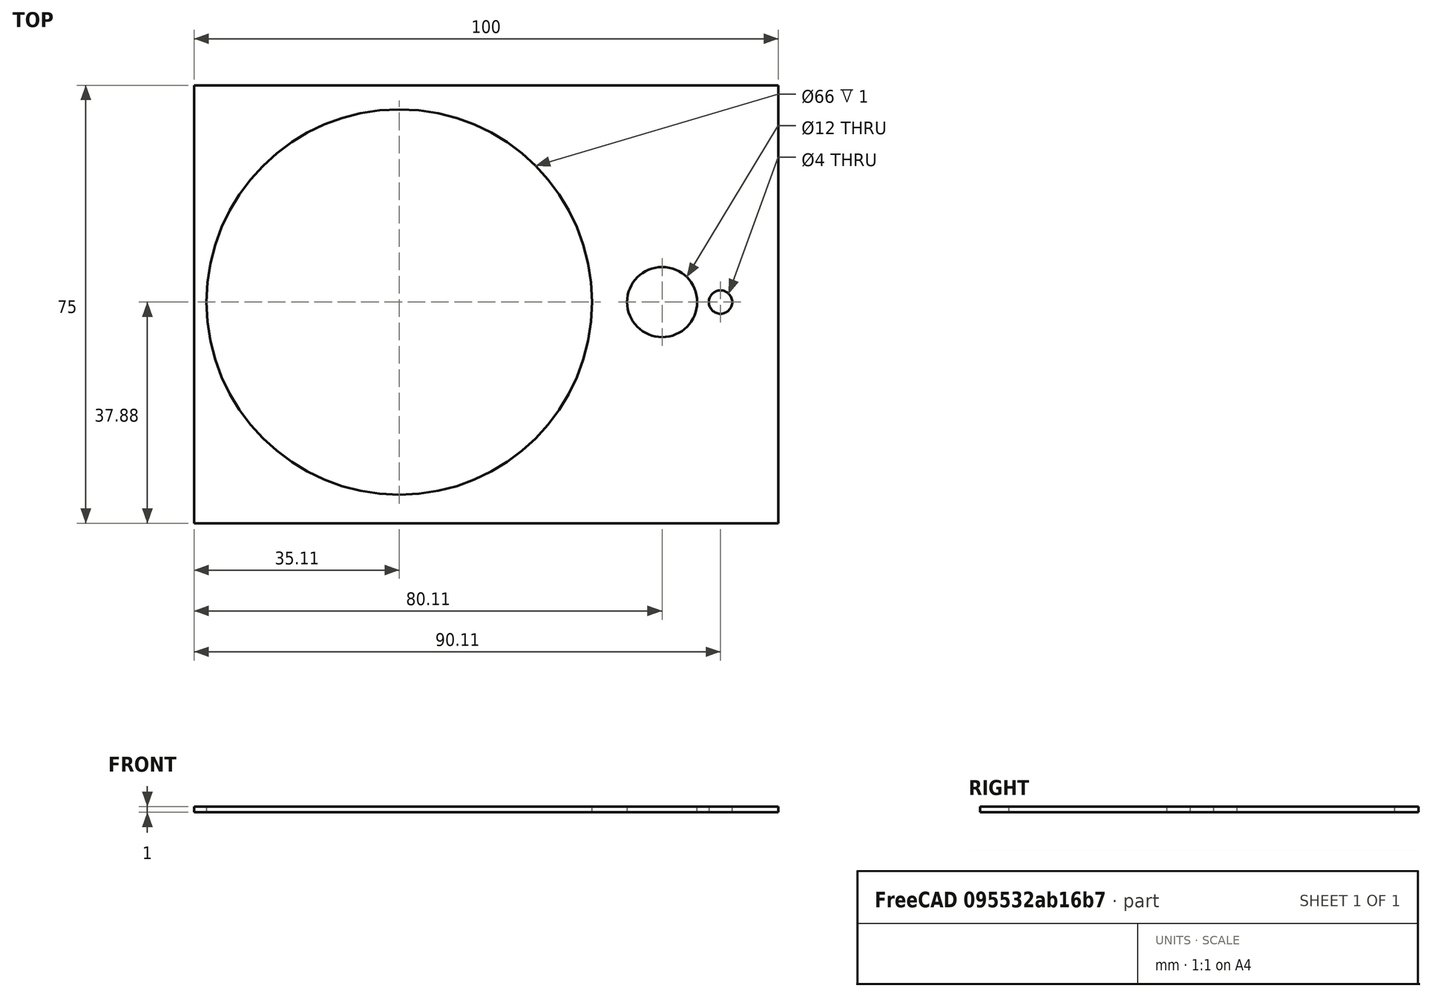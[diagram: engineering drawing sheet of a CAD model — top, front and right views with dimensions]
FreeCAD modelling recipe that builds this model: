
FCSTD DOCUMENT  (FreeCAD 0.19R24366 (Git))
Label: cpu switches
License: All rights reserved
LicenseURL: http://en.wikipedia.org/wiki/All_rights_reserved
objects: Sketcher::SketchObject×1, PartDesign::Pad×1, PartDesign::Body×1
note: 4 computed .brp shape members not serialized (recipe doc carries the construction recipe); baked Part::Feature solids carry a one-line shape summary decoded from their .brp

FEATURE [Sketcher::SketchObject] Sketch
  FullyConstrained = false
  MapMode = 5
  Support = -> [XY_Plane]
  sketch-geometry (8):
    g0: LineSegment StartX=-35.1106 StartY=37.1163 StartZ=0 EndX=64.8894 EndY=37.1163 EndZ=0
    g1: LineSegment StartX=64.8894 StartY=37.1163 StartZ=0 EndX=64.8894 EndY=-37.8837 EndZ=0
    g2: LineSegment StartX=64.8894 StartY=-37.8837 StartZ=0 EndX=-35.1106 EndY=-37.8837 EndZ=0
    g3: LineSegment StartX=-35.1106 StartY=-37.8837 StartZ=0 EndX=-35.1106 EndY=37.1163 EndZ=0
    g4: Circle CenterX=0 CenterY=0 CenterZ=0 NormalX=0 NormalY=0 NormalZ=1 AngleXU=0 Radius=32.5
    g5: Circle CenterX=45 CenterY=0 CenterZ=0 NormalX=0 NormalY=0 NormalZ=1 AngleXU=0 Radius=6
    g6: Circle CenterX=55 CenterY=0 CenterZ=0 NormalX=0 NormalY=0 NormalZ=1 AngleXU=0 Radius=2
    g7: GeomPoint X=32.5 Y=0.00546977 Z=0
  constraints (19):
    c: Coincident(g0,g1)
    c: Coincident(g1,g2)
    c: Coincident(g2,g3)
    c: Coincident(g3,g0)
    c: Horizontal(g0)
    c: Horizontal(g2)
    c: Vertical(g1)
    c: Vertical(g3)
    c: DistanceX(g0,g0) = 100
    c: DistanceY(g3,g3) = 75
    c: Radius(g4) = 32.5
    c: Coincident(g4,g-1)
    c: PointOnObject(g5,g-1)
    c: Radius(g5) = 6
    c: PointOnObject(g6,g-1)
    c: Radius(g6) = 2
    c: PointOnObject(g7,g4)
    c: DistanceX(g4,g5) = 45
    c: DistanceX(g4,g6) = 55
FEATURE [PartDesign::Pad] Pad
  Direction = (1,1,1)
  Length = 1
  Length2 = 100
  Profile = -> Sketch
  Type = 0
FEATURE [PartDesign::Body] Body
  Group = -> [Sketch,Pad]
  Origin = -> Origin
  Tip = -> Pad
